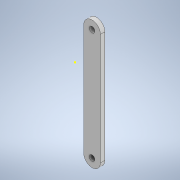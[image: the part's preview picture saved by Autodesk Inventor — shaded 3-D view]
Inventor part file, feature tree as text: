
AUTODESK INVENTOR PART (.ipt)
format: ipt  version: 2022 (Build 260153000, 153)  size: 103,936 bytes
history: native  units: in
note: dims shown in document units (in); Inventor stores cm internally (conversion verified against a paired STEP export)
features: sketch x2, extrude x1
ambient origin geometry x8: Origin, YZ Plane, XZ Plane, XY Plane, X Axis, Y Axis, Z Axis, Center Point
bodies: Solid1 (feature_tree)
feature tree (3):
  extrude  "Extrusion1"  Depth=0.5906in
  sketch  "Sketch2"  dims[d2=0.1969in d3=0.1575in d4=0.0in]
  sketch  "Sketch1"  dims[d0=3.937in d1=0.5906in]
